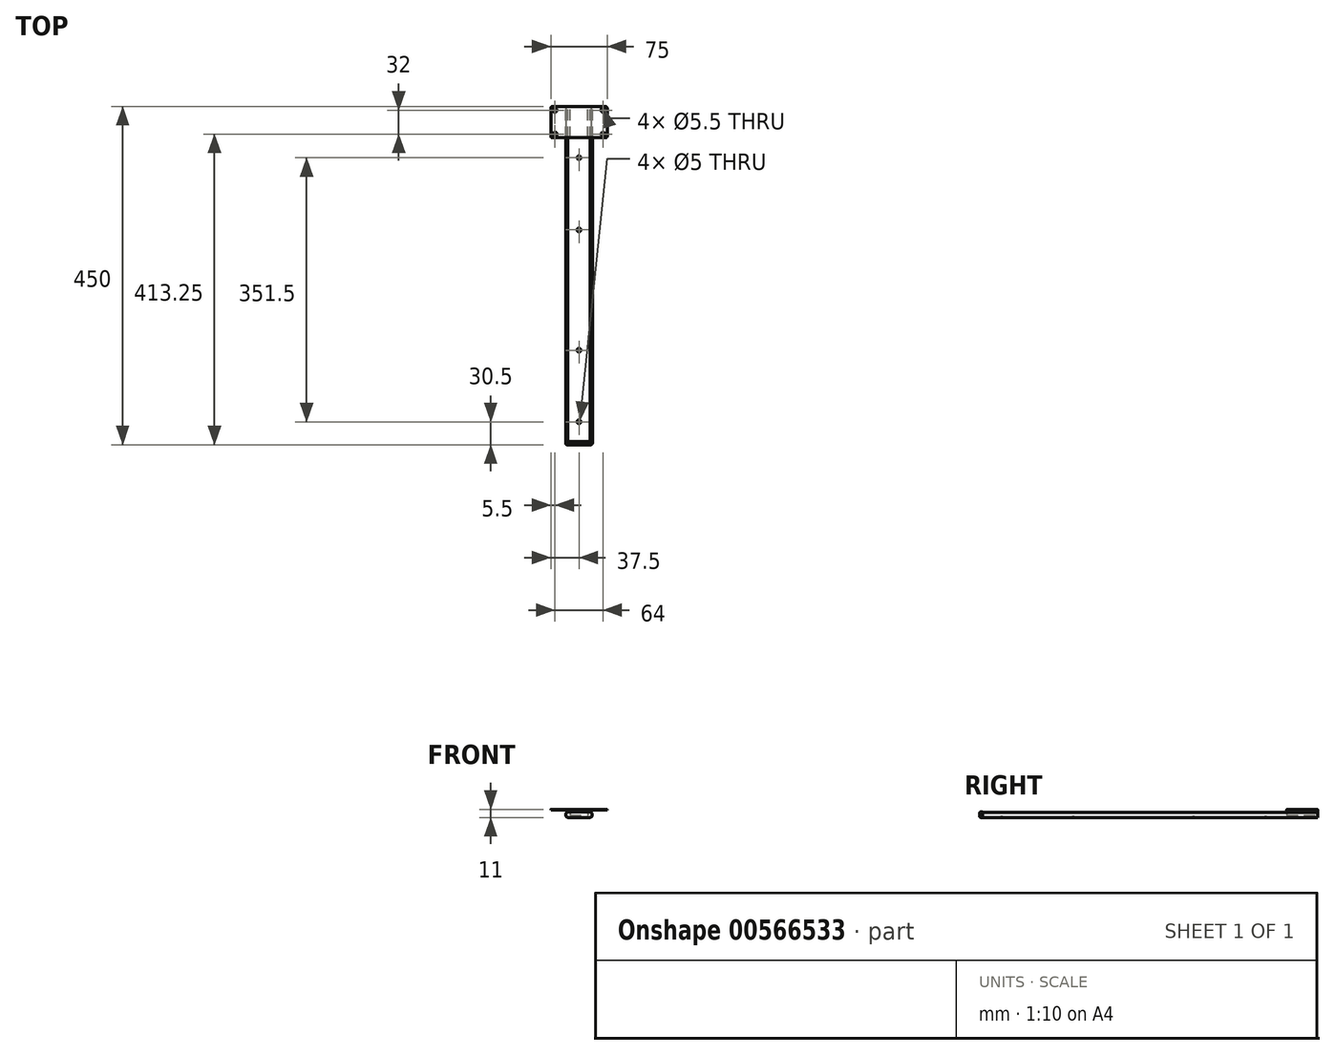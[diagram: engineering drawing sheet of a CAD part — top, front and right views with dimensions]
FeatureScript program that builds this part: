
annotation { "Feature Type Name" : "Feature", "Feature Type Description" : "" }
export const myFeature = defineFeature(function(context is Context, id is Id, definition is map)
    precondition{}
    {
        {
            var Q0;
            Q0=qCreatedBy(makeId("Front.planeOp"),FACE);
            var sketch = newSketch(context, id + "F0", { "sketchPlane" : qUnion([Q0])});
            skLineSegment(sketch, "E0", {"start": v(0, -5.25) * mm, "end": v(-14, -5.25) * mm});
            skArc(sketch, "E1", {"start": v(-14, -5.25) * mm, "mid": v(-17.67, -2.26) * mm, "end": v(-15.5, 1.94) * mm});
            skLineSegment(sketch, "E2.MirrorCS", {"start": v(0, -5.25) * mm, "end": v(14, -5.25) * mm});
            skArc(sketch, "E3.MirrorCS", {"start": v(14, -5.25) * mm, "mid": v(17.67, -2.26) * mm, "end": v(15.5, 1.94) * mm});
            skLineSegment(sketch, "E4", {"start": v(-15.5, 1.94) * mm, "end": v(-14, -1.5) * mm, "construction": true});
            skLineSegment(sketch, "E5", {"start": v(-15.5, 1.94) * mm, "end": v(-15.1, 1.02) * mm});
            skLineSegment(sketch, "E6", {"start": v(-14, -4.25) * mm, "end": v(14, -4.25) * mm});
            skLineSegment(sketch, "E7.MirrorCS", {"start": v(15.5, 1.94) * mm, "end": v(14, -1.5) * mm, "construction": true});
            skLineSegment(sketch, "E8.MirrorCS", {"start": v(15.5, 1.94) * mm, "end": v(15.1, 1.02) * mm});
            skArc(sketch, "E9", {"start": v(-14, -4.25) * mm, "mid": v(-16.7, -2.06) * mm, "end": v(-15.1, 1.02) * mm});
            skArc(sketch, "E10", {"start": v(14, -4.25) * mm, "mid": v(16.7, -2.06) * mm, "end": v(15.1, 1.02) * mm});
            skPoint(sketch, "E11", {"position": v(0, -2.25) * mm});
            skSolve(sketch);
        }
        {
            var Q0;
            Q0=qCreatedBy(makeId("Front.planeOp"),FACE);
            var sketch = newSketch(context, id + "F1", { "sketchPlane" : qUnion([Q0])});
            skLineSegment(sketch, "E12", {"start": v(-37.5, 5.75) * mm, "end": v(-37.5, 4.95) * mm});
            skLineSegment(sketch, "E13", {"start": v(-37.5, 4.95) * mm, "end": v(-12, 4.95) * mm});
            skLineSegment(sketch, "E14", {"start": v(-12, 4.95) * mm, "end": v(-12, -2.05) * mm});
            skLineSegment(sketch, "E15", {"start": v(-12, -2.05) * mm, "end": v(0, -2.05) * mm});
            skLineSegment(sketch, "E16", {"start": v(-37.5, 5.75) * mm, "end": v(0, 5.75) * mm});
            skLineSegment(sketch, "E17.MirrorCS", {"start": v(37.5, 5.75) * mm, "end": v(0, 5.75) * mm});
            skLineSegment(sketch, "E18.MirrorCS", {"start": v(37.5, 4.95) * mm, "end": v(12, 4.95) * mm});
            skLineSegment(sketch, "E19.MirrorCS", {"start": v(37.5, 5.75) * mm, "end": v(37.5, 4.95) * mm});
            skLineSegment(sketch, "E20.MirrorCS", {"start": v(12, 4.95) * mm, "end": v(12, -2.05) * mm});
            skLineSegment(sketch, "E21.MirrorCS", {"start": v(12, -2.05) * mm, "end": v(0, -2.05) * mm});
            skPoint(sketch, "E22", {"position": v(0, -2.25) * mm});
            skSolve(sketch);
        }
        {
            var Q0;
            Q0 = qSketchRegion(id + "F1", true);
            extrude(context, id + "F2", {"entities" : qUnion([Q0]), "depth" : 41.5 * mm, "offsetDistance" : 25 * mm});
        }
        {
            var Q0;
            Q0=makeQuery(id+"F2.opExtrude","CAP_EDGE",EDGE,{"disambiguationData":[OSD([sQuery(id+"F1.wireOp",EDGE,"E19.MirrorCS")])],"isStart":true});
            var Q1;
            Q1=makeQuery(id+"F2.opExtrude","CAP_EDGE",EDGE,{"disambiguationData":[OSD([sQuery(id+"F1.wireOp",EDGE,"E12")])],"isStart":true});
            var Q2;
            Q2=makeQuery(id+"F2.opExtrude","CAP_EDGE",EDGE,{"disambiguationData":[OSD([sQuery(id+"F1.wireOp",EDGE,"E12")])],"isStart":false});
            var Q3;
            Q3=makeQuery(id+"F2.opExtrude","CAP_EDGE",EDGE,{"disambiguationData":[OSD([sQuery(id+"F1.wireOp",EDGE,"E19.MirrorCS")])],"isStart":false});
            fillet(context, id + "F3", {"entities" : qUnion([Q0, Q1, Q2, Q3]), "radius" : 2 * mm, "tangentPropagation" : true, "allowEdgeOverflow" : false});
        }
        {
            var Q0;
            Q0 = qSketchRegion(id + "F0", true);
            extrude(context, id + "F4", {"entities" : qUnion([Q0]), "depth" : 446 * mm, "offsetDistance" : 25 * mm});
        }
        {
            var Q0;
            Q0=makeQuery(id+"F4.opExtrude","SWEPT_FACE",FACE,{"disambiguationData":[OSD([sQuery(id+"F0.wireOp",EDGE,"E0"),sQuery(id+"F0.wireOp",EDGE,"E2.MirrorCS")])]});
            var sketch = newSketch(context, id + "F5", { "sketchPlane" : qUnion([Q0])});
            skPoint(sketch, "E23", {"position": v(0, 68) * mm});
            skPoint(sketch, "E24", {"position": v(0, 164) * mm});
            skPoint(sketch, "E25", {"position": v(0, 324.25) * mm});
            skPoint(sketch, "E26", {"position": v(0, 419.5) * mm});
            skSolve(sketch);
        }
        {
            var Q0;
            Q0=makeQuery(id+"F2.opExtrude","SWEPT_FACE",FACE,{"disambiguationData":[OSD([sQuery(id+"F1.wireOp",EDGE,"E16"),sQuery(id+"F1.wireOp",EDGE,"E17.MirrorCS")])]});
            var sketch = newSketch(context, id + "F6", { "sketchPlane" : qUnion([Q0])});
            skLineSegment(sketch, "E27", {"start": v(-32, 0) * mm, "end": v(-32, -53.86) * mm, "construction": true});
            skLineSegment(sketch, "E28", {"start": v(32, 0) * mm, "end": v(32, -56) * mm, "construction": true});
            skPoint(sketch, "E29", {"position": v(-21.09, 0) * mm});
            skLineSegment(sketch, "E30", {"start": v(0, 0) * mm, "end": v(0, -41.5) * mm, "construction": true});
            skPoint(sketch, "E31", {"position": v(0, -20.75) * mm});
            skLineSegment(sketch, "E32", {"start": v(-37.5, -20.75) * mm, "end": v(37.5, -20.75) * mm, "construction": true});
            skLineSegment(sketch, "E33", {"start": v(-37.5, -4.75) * mm, "end": v(37.5, -4.75) * mm, "construction": true});
            skLineSegment(sketch, "E34", {"start": v(-37.5, -36.75) * mm, "end": v(37.5, -36.75) * mm, "construction": true});
            skPoint(sketch, "E35", {"position": v(-32, -4.75) * mm});
            skPoint(sketch, "E36", {"position": v(-32, -36.75) * mm});
            skPoint(sketch, "E37", {"position": v(32, -36.75) * mm});
            skPoint(sketch, "E38", {"position": v(32, -4.75) * mm});
            skSolve(sketch);
        }
        {
            var Q0;
            Q0=sQuery(id+"F6.wireOp",VERTEX,"E35");
            var Q1;
            Q1=sQuery(id+"F6.wireOp",VERTEX,"E36");
            var Q2;
            Q2=sQuery(id+"F6.wireOp",VERTEX,"E37");
            var Q3;
            Q3=sQuery(id+"F6.wireOp",VERTEX,"E38");
            var Q4;
            Q4=makeQuery(id+"F2.opExtrude","SWEPT_BODY",BODY,{"disambiguationData":[OSD([sQuery(id+"F1.wireOp",EDGE,"E12"),sQuery(id+"F1.wireOp",EDGE,"E13"),sQuery(id+"F1.wireOp",EDGE,"E14"),sQuery(id+"F1.wireOp",EDGE,"E15"),sQuery(id+"F1.wireOp",EDGE,"E16"),sQuery(id+"F1.wireOp",EDGE,"E17.MirrorCS"),sQuery(id+"F1.wireOp",EDGE,"E18.MirrorCS"),sQuery(id+"F1.wireOp",EDGE,"E19.MirrorCS"),sQuery(id+"F1.wireOp",EDGE,"E20.MirrorCS"),sQuery(id+"F1.wireOp",EDGE,"E21.MirrorCS")])]});
            hole(context, id + "F7", {"style" : HoleStyle.SIMPLE, "endStyle" : HoleEndStyle.BLIND, "holeDiameter" : 5.5 * mm, "majorDiameter" : 5 * mm, "holeDepth" : 7.5 * mm, "isTappedThrough" : true, "tappedDepth" : 12 * mm, "tapClearance" : 3, "locations" : qUnion([Q0, Q1, Q2, Q3]), "scope" : qUnion([Q4])});
        }
        {
            var Q0;
            Q0=sQuery(id+"F5.wireOp",VERTEX,"E23");
            var Q1;
            Q1=sQuery(id+"F5.wireOp",VERTEX,"E24");
            var Q2;
            Q2=sQuery(id+"F5.wireOp",VERTEX,"E26");
            var Q3;
            Q3=sQuery(id+"F5.wireOp",VERTEX,"E25");
            var Q4;
            Q4=makeQuery(id+"F4.opExtrude","SWEPT_BODY",BODY,{"disambiguationData":[OSD([sQuery(id+"F0.wireOp",EDGE,"E0"),sQuery(id+"F0.wireOp",EDGE,"E1"),sQuery(id+"F0.wireOp",EDGE,"E2.MirrorCS"),sQuery(id+"F0.wireOp",EDGE,"E5"),sQuery(id+"F0.wireOp",EDGE,"E6"),sQuery(id+"F0.wireOp",EDGE,"E8.MirrorCS"),sQuery(id+"F0.wireOp",EDGE,"E3.MirrorCS"),sQuery(id+"F0.wireOp",EDGE,"E9"),sQuery(id+"F0.wireOp",EDGE,"E10")])]});
            hole(context, id + "F8", {"style" : HoleStyle.SIMPLE, "endStyle" : HoleEndStyle.BLIND, "holeDiameter" : 5 * mm, "majorDiameter" : 5 * mm, "holeDepth" : 7.5 * mm, "isTappedThrough" : true, "tappedDepth" : 12 * mm, "tapClearance" : 3, "locations" : qUnion([Q0, Q1, Q2, Q3]), "scope" : qUnion([Q4])});
        }
        {
            var Q0;
            Q0=qCreatedBy(makeId("Front.planeOp"),FACE);
            var sketch = newSketch(context, id + "F9", { "sketchPlane" : qUnion([Q0])});
            skPoint(sketch, "E39", {"position": v(0, -2.25) * mm});
            skLineSegment(sketch, "E40", {"start": v(-14, -5.25) * mm, "end": v(-14, 3.8) * mm, "construction": true});
            skLineSegment(sketch, "E41", {"start": v(14, -5.25) * mm, "end": v(14, 3.51) * mm, "construction": true});
            skArc(sketch, "E42", {"start": v(-14, -5.25) * mm, "mid": v(-17.75, -1.5) * mm, "end": v(-14, 2.25) * mm});
            skLineSegment(sketch, "E43", {"start": v(-14, 2.25) * mm, "end": v(14, 2.25) * mm});
            skArc(sketch, "E44", {"start": v(14, 2.25) * mm, "mid": v(17.75, -1.5) * mm, "end": v(14, -5.25) * mm});
            skLineSegment(sketch, "E45", {"start": v(-14, -5.25) * mm, "end": v(14, -5.25) * mm});
            skSolve(sketch);
        }
        {
            var Q0;
            Q0 = qSketchRegion(id + "F9", true);
            extrude(context, id + "F10", {"entities" : qUnion([Q0]), "oppositeDirection" : true, "depth" : 4 * mm, "offsetDistance" : 25 * mm});
        }
        {
            var Q0;
            Q0=makeQuery(id+"F10.opExtrude","SWEPT_BODY",BODY,{"disambiguationData":[OSD([sQuery(id+"F9.wireOp",EDGE,"E42"),sQuery(id+"F9.wireOp",EDGE,"E43"),sQuery(id+"F9.wireOp",EDGE,"E44"),sQuery(id+"F9.wireOp",EDGE,"E45")])]});
            var Q1;
            Q1=makeQuery(id+"F4.opExtrude","SWEPT_EDGE",EDGE,{"disambiguationData":[OSD([sQuery(id+"F0.wireOp",EDGE,"E0"),sQuery(id+"F0.wireOp",EDGE,"E1")])]});
            var Q2;
            Q2=makeQuery(id+"F4.opExtrude","SWEPT_EDGE",EDGE,{"disambiguationData":[OSD([sQuery(id+"F0.wireOp",EDGE,"E8.MirrorCS"),sQuery(id+"F0.wireOp",EDGE,"E3.MirrorCS")])]});
            transform(context, id + "F11", {"entities" : qUnion([Q0]), "transformType" : TransformType.TRANSLATION_DISTANCE, "transformDirection" : qUnion([Q2]), "distance" : 450 * mm, "oppositeDirection" : true, "makeCopy" : false});
        }
        {
            var Q0;
            Q0=makeQuery(id+"F10.opExtrude","CAP_FACE",FACE,{"disambiguationData":[OSD([sQuery(id+"F9.wireOp",EDGE,"E42"),sQuery(id+"F9.wireOp",EDGE,"E43"),sQuery(id+"F9.wireOp",EDGE,"E44"),sQuery(id+"F9.wireOp",EDGE,"E45")])],"isStart":true});
            fillet(context, id + "F12", {"entities" : qUnion([Q0]), "radius" : 2 * mm, "tangentPropagation" : true, "allowEdgeOverflow" : false});
        }
    });
